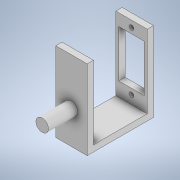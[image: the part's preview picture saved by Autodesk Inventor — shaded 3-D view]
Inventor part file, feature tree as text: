
AUTODESK INVENTOR PART (.ipt)
format: ipt  version: 2020.3 (Build 243373000, 373)  size: 150,016 bytes
history: native  units: mm
features: extrude x4, sketch x4
ambient origin geometry x8: Origin, YZ Plane, XZ Plane, XY Plane, X Axis, Y Axis, Z Axis, Center Point
bodies: Solid1 (feature_tree)
feature tree (8):
  extrude  "Extrusion1"  Depth=3.0mm
  extrude  "Extrusion2"  Depth=35.0mm TaperAngle=0.0deg
  extrude  "Extrusion3"  Depth=10.0mm TaperAngle=0.0deg
  extrude  "Extrusion5"  [1 undecoded]
  sketch  "Sketch1"  dims[d3=3.0mm d4=0.0mm d5=3.0mm]
  sketch  "Sketch2"  dims[d6=3.0mm d7=35.0mm d8=0.0mm]
  sketch  "Sketch4"  dims[d9=2.0mm d10=10.0mm d11=0.0mm]
  sketch  "Sketch6"  dims[d15=14.0mm d16=0.0mm]
note: 1 required parameter value undecoded (feature->parameter linkage not recoverable at this tier; creation-order binding heuristic only, values carry confidence <= 0.55)
